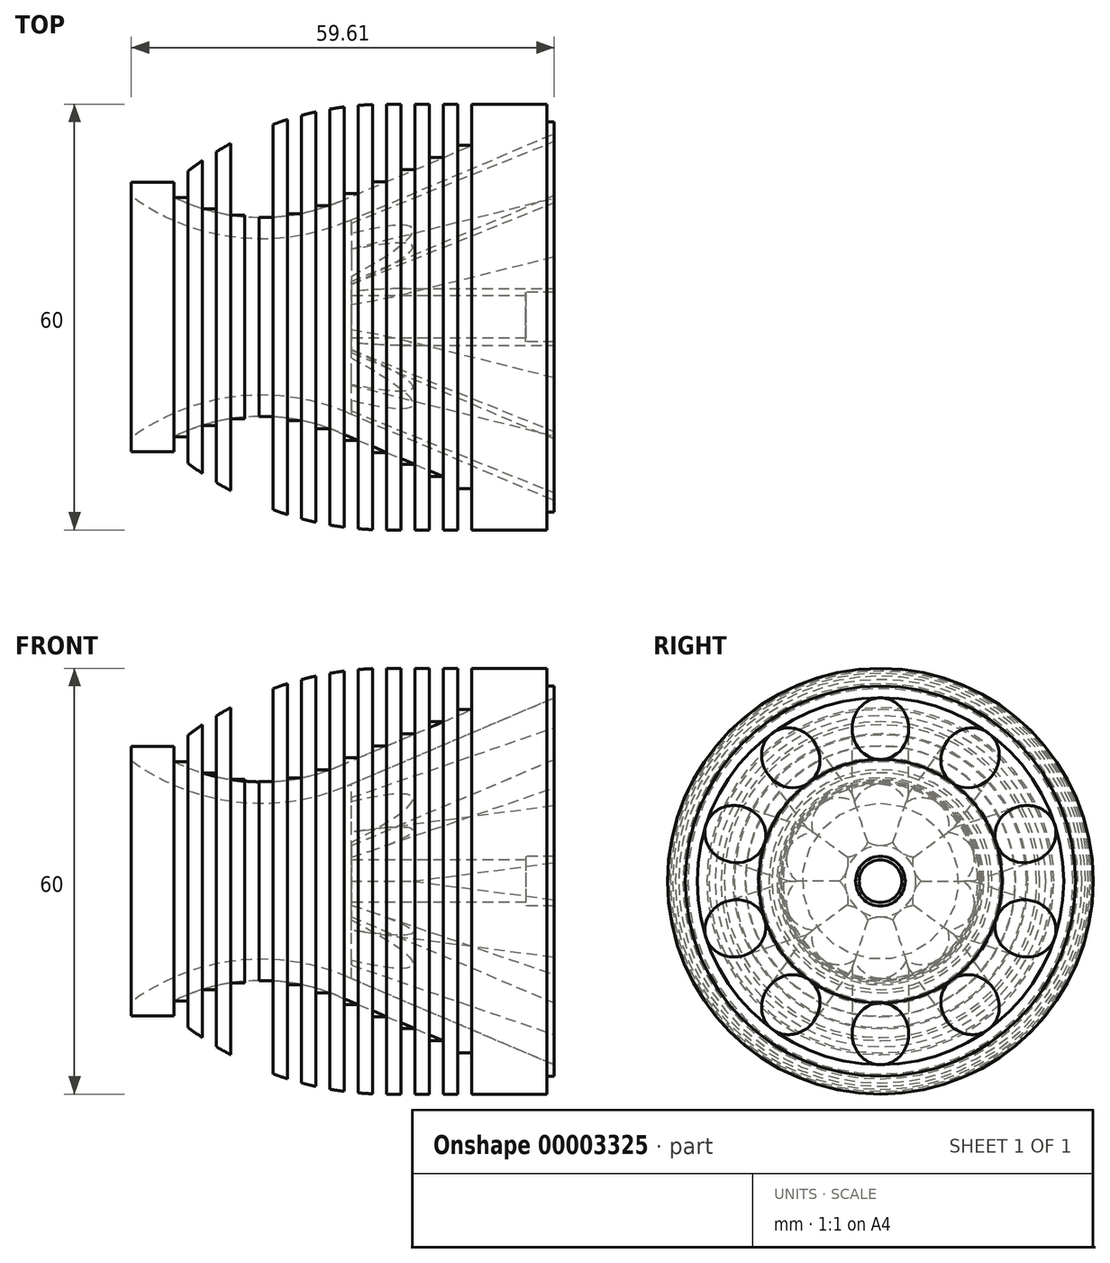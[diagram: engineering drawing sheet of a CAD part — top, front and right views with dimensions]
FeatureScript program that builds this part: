
annotation { "Feature Type Name" : "Feature", "Feature Type Description" : "" }
export const myFeature = defineFeature(function(context is Context, id is Id, definition is map)
    precondition{}
    {
        {
            var Q0;
            Q0=qCreatedBy(makeId("Front.planeOp"),FACE);
            var sketch = newSketch(context, id + "F0", { "sketchPlane" : qUnion([Q0])});
            skLineSegment(sketch, "E0", {"start": v(0, 0) * mm, "end": v(59.61, 0) * mm, "construction": true});
            skLineSegment(sketch, "E1", {"start": v(59.61, 27.5) * mm, "end": v(59.61, -27.5) * mm});
            skLineSegment(sketch, "E2", {"start": v(59.61, 27.5) * mm, "end": v(58.61, 27.5) * mm});
            skLineSegment(sketch, "E3", {"start": v(58.61, 27.5) * mm, "end": v(58.61, 30) * mm});
            skLineSegment(sketch, "E4.0.MirrorCS", {"start": v(58.61, -27.5) * mm, "end": v(58.61, -30) * mm});
            skLineSegment(sketch, "E5.0.MirrorCS", {"start": v(59.61, -27.5) * mm, "end": v(58.61, -27.5) * mm});
            skLineSegment(sketch, "E6", {"start": v(58.61, 30) * mm, "end": v(48, 30) * mm});
            skLineSegment(sketch, "E7.0.MirrorCS", {"start": v(58.61, -30) * mm, "end": v(48, -30) * mm});
            skLineSegment(sketch, "E8", {"start": v(0, 17) * mm, "end": v(0, -17) * mm});
            skLineSegment(sketch, "E9", {"start": v(59.61, 3.5) * mm, "end": v(55.61, 3.5) * mm});
            skLineSegment(sketch, "E10", {"start": v(55.61, 3.5) * mm, "end": v(55.61, 3) * mm});
            skLineSegment(sketch, "E11", {"start": v(55.61, 3) * mm, "end": v(31, 3) * mm});
            skLineSegment(sketch, "E12", {"start": v(31, 3) * mm, "end": v(31, 5) * mm});
            skLineSegment(sketch, "E13", {"start": v(31, 5) * mm, "end": v(59.61, 17.15) * mm});
            skLineSegment(sketch, "E14", {"start": v(59.61, 25.85) * mm, "end": v(30.44, 13.46) * mm});
            skLineSegment(sketch, "E15.0.MirrorCS", {"start": v(59.61, -3.5) * mm, "end": v(55.61, -3.5) * mm});
            skLineSegment(sketch, "E16.0.MirrorCS", {"start": v(55.61, -3.5) * mm, "end": v(55.61, -3) * mm});
            skLineSegment(sketch, "E17.0.MirrorCS", {"start": v(55.61, -3) * mm, "end": v(31, -3) * mm});
            skLineSegment(sketch, "E18.0.MirrorCS", {"start": v(31, -3) * mm, "end": v(31, -5) * mm});
            skLineSegment(sketch, "E19.0.MirrorCS", {"start": v(31, -5) * mm, "end": v(59.61, -17.15) * mm});
            skLineSegment(sketch, "E20.0.MirrorCS", {"start": v(59.61, -25.85) * mm, "end": v(30.44, -13.46) * mm});
            skArc(sketch, "E21", {"start": v(30.44, 13.46) * mm, "mid": v(14.75, 11.2) * mm, "end": v(0, 17) * mm});
            skArc(sketch, "E22.0.MirrorCS", {"start": v(30.44, -13.46) * mm, "mid": v(14.75, -11.2) * mm, "end": v(0, -17) * mm});
            skArc(sketch, "E23.0", {"start": v(29.27, 16.23) * mm, "mid": v(17.57, 14.01) * mm, "end": v(6, 16.86) * mm});
            skLineSegment(sketch, "E23.1", {"start": v(48, 24.18) * mm, "end": v(29.27, 16.23) * mm});
            skLineSegment(sketch, "E24", {"start": v(0, 17) * mm, "end": v(0, 19) * mm});
            skLineSegment(sketch, "E25.0.MirrorCS", {"start": v(48, -24.18) * mm, "end": v(29.27, -16.23) * mm});
            skArc(sketch, "E26.0.MirrorCS", {"start": v(29.27, -16.23) * mm, "mid": v(17.57, -14.01) * mm, "end": v(6, -16.86) * mm});
            skLineSegment(sketch, "E27.0.MirrorCS", {"start": v(0, -17) * mm, "end": v(0, -19) * mm});
            skLineSegment(sketch, "E28", {"start": v(48, 30) * mm, "end": v(48, 24.18) * mm});
            skLineSegment(sketch, "E29.0.MirrorCS", {"start": v(48, -30) * mm, "end": v(48, -24.18) * mm});
            skLineSegment(sketch, "E30", {"start": v(6, -19) * mm, "end": v(6, -16.86) * mm});
            skLineSegment(sketch, "E31.0.MirrorCS", {"start": v(6, 19) * mm, "end": v(6, 16.86) * mm});
            skLineSegment(sketch, "E32", {"start": v(0, 19) * mm, "end": v(6, 19) * mm});
            skLineSegment(sketch, "E33.0.MirrorCS", {"start": v(0, -19) * mm, "end": v(6, -19) * mm});
            skLineSegment(sketch, "E34", {"start": v(31, 5) * mm, "end": v(31, 13.7) * mm});
            skLineSegment(sketch, "E35.0.MirrorCS", {"start": v(31, -5) * mm, "end": v(31, -13.7) * mm});
            skPoint(sketch, "E36", {"position": v(31, 9.36) * mm});
            skLineSegment(sketch, "E37", {"start": v(25.3, 6.93) * mm, "end": v(66.16, 24.28) * mm, "construction": true});
            skPoint(sketch, "E38", {"position": v(59.61, 21.5) * mm});
            skPoint(sketch, "E39.0.MirrorP", {"position": v(59.61, -21.5) * mm});
            skSolve(sketch);
        }
        {
            var Q0;
            Q0=qCreatedBy(makeId("Front.planeOp"),FACE);
            var sketch = newSketch(context, id + "F1", { "sketchPlane" : qUnion([Q0])});
            skLineSegment(sketch, "E40.0", {"start": v(48, 30) * mm, "end": v(48, 24.18) * mm});
            skLineSegment(sketch, "E40.1", {"start": v(48, 24.18) * mm, "end": v(29.27, 16.23) * mm});
            skArc(sketch, "E40.2", {"start": v(29.27, 16.23) * mm, "mid": v(17.57, 14.01) * mm, "end": v(6, 16.86) * mm});
            skLineSegment(sketch, "E40.5", {"start": v(58.61, 30) * mm, "end": v(48, 30) * mm});
            skLineSegment(sketch, "E41", {"start": v(48, 30) * mm, "end": v(36, 30) * mm});
            skArc(sketch, "E42", {"start": v(36, 30) * mm, "mid": v(20.02, 27.16) * mm, "end": v(6, 19) * mm});
            skLineSegment(sketch, "E43", {"start": v(8, 15.98) * mm, "end": v(8, 20.6) * mm});
            skLineSegment(sketch, "E44", {"start": v(10, 15.27) * mm, "end": v(10, 22.03) * mm});
            skLineSegment(sketch, "E45", {"start": v(12, 14.72) * mm, "end": v(12, 23.31) * mm});
            skLineSegment(sketch, "E46", {"start": v(14, 14.34) * mm, "end": v(14, 24.45) * mm});
            skLineSegment(sketch, "E47", {"start": v(16, 14.1) * mm, "end": v(16, 25.47) * mm});
            skLineSegment(sketch, "E48", {"start": v(18, 14) * mm, "end": v(18, 26.37) * mm});
            skLineSegment(sketch, "E49", {"start": v(20, 14.05) * mm, "end": v(20, 27.15) * mm});
            skLineSegment(sketch, "E50", {"start": v(22, 14.24) * mm, "end": v(22, 27.84) * mm});
            skLineSegment(sketch, "E51", {"start": v(24, 14.58) * mm, "end": v(24, 28.42) * mm});
            skLineSegment(sketch, "E52", {"start": v(26, 15.07) * mm, "end": v(26, 28.9) * mm});
            skLineSegment(sketch, "E53", {"start": v(8, 20.6) * mm, "end": v(10, 20.6) * mm, "construction": true});
            skLineSegment(sketch, "E54", {"start": v(10, 22.03) * mm, "end": v(12, 22.03) * mm, "construction": true});
            skLineSegment(sketch, "E55", {"start": v(12, 23.31) * mm, "end": v(14, 23.31) * mm, "construction": true});
            skLineSegment(sketch, "E56", {"start": v(14, 24.45) * mm, "end": v(16, 24.45) * mm, "construction": true});
            skLineSegment(sketch, "E57", {"start": v(16, 25.47) * mm, "end": v(18, 25.47) * mm, "construction": true});
            skLineSegment(sketch, "E58", {"start": v(18, 26.37) * mm, "end": v(20, 26.37) * mm, "construction": true});
            skLineSegment(sketch, "E59", {"start": v(20, 27.15) * mm, "end": v(22, 27.15) * mm, "construction": true});
            skLineSegment(sketch, "E60", {"start": v(22, 27.84) * mm, "end": v(24, 27.84) * mm, "construction": true});
            skLineSegment(sketch, "E61", {"start": v(24, 28.42) * mm, "end": v(26, 28.42) * mm, "construction": true});
            skLineSegment(sketch, "E62", {"start": v(28, 29.3) * mm, "end": v(28, 15.72) * mm});
            skLineSegment(sketch, "E63", {"start": v(32, 29.83) * mm, "end": v(32, 17.38) * mm});
            skLineSegment(sketch, "E64", {"start": v(34, 29.96) * mm, "end": v(34, 18.23) * mm});
            skLineSegment(sketch, "E65", {"start": v(36, 30) * mm, "end": v(36, 19.08) * mm});
            skLineSegment(sketch, "E66", {"start": v(38, 30) * mm, "end": v(38, 19.93) * mm});
            skLineSegment(sketch, "E67", {"start": v(40, 30) * mm, "end": v(40, 20.78) * mm});
            skLineSegment(sketch, "E68", {"start": v(42, 30) * mm, "end": v(42, 21.63) * mm});
            skLineSegment(sketch, "E69", {"start": v(26, 22) * mm, "end": v(28, 22) * mm, "construction": true});
            skLineSegment(sketch, "E70", {"start": v(28, 22.51) * mm, "end": v(30, 22.51) * mm, "construction": true});
            skLineSegment(sketch, "E71", {"start": v(30, 23.07) * mm, "end": v(32, 23.07) * mm, "construction": true});
            skLineSegment(sketch, "E72", {"start": v(32, 23.6) * mm, "end": v(34, 23.6) * mm, "construction": true});
            skLineSegment(sketch, "E73", {"start": v(34, 24.1) * mm, "end": v(36, 24.1) * mm, "construction": true});
            skLineSegment(sketch, "E74", {"start": v(36, 24.54) * mm, "end": v(38, 24.54) * mm, "construction": true});
            skLineSegment(sketch, "E75", {"start": v(38, 24.97) * mm, "end": v(40, 24.97) * mm, "construction": true});
            skLineSegment(sketch, "E76", {"start": v(40, 25.4) * mm, "end": v(42, 25.4) * mm, "construction": true});
            skLineSegment(sketch, "E77", {"start": v(44, 22.48) * mm, "end": v(44, 30) * mm});
            skLineSegment(sketch, "E78", {"start": v(46, 23.33) * mm, "end": v(46, 30) * mm});
            skLineSegment(sketch, "E79", {"start": v(42, 25.81) * mm, "end": v(44, 25.81) * mm, "construction": true});
            skLineSegment(sketch, "E80", {"start": v(44, 26.24) * mm, "end": v(46, 26.24) * mm, "construction": true});
            skLineSegment(sketch, "E81.0", {"start": v(6, 19) * mm, "end": v(6, 16.86) * mm});
            skLineSegment(sketch, "E81.1", {"start": v(0, 19) * mm, "end": v(6, 19) * mm});
            skLineSegment(sketch, "E81.2", {"start": v(0, 17) * mm, "end": v(0, 19) * mm});
            skLineSegment(sketch, "E82", {"start": v(30, 29.61) * mm, "end": v(30, 16.54) * mm});
            skLineSegment(sketch, "E83", {"start": v(6, 16.86) * mm, "end": v(8, 16.86) * mm});
            skLineSegment(sketch, "E84", {"start": v(10, 15.27) * mm, "end": v(12, 15.27) * mm});
            skLineSegment(sketch, "E85", {"start": v(14, 14.34) * mm, "end": v(16, 14.34) * mm});
            skLineSegment(sketch, "E86", {"start": v(20, 14.05) * mm, "end": v(18, 14.05) * mm});
            skLineSegment(sketch, "E87", {"start": v(24, 14.58) * mm, "end": v(22, 14.58) * mm});
            skLineSegment(sketch, "E88", {"start": v(28, 15.72) * mm, "end": v(26, 15.72) * mm});
            skLineSegment(sketch, "E89", {"start": v(32, 17.38) * mm, "end": v(30, 17.38) * mm});
            skLineSegment(sketch, "E90", {"start": v(36, 19.08) * mm, "end": v(34, 19.08) * mm});
            skLineSegment(sketch, "E91", {"start": v(40, 20.78) * mm, "end": v(38, 20.78) * mm});
            skLineSegment(sketch, "E92", {"start": v(44, 22.48) * mm, "end": v(42, 22.48) * mm});
            skLineSegment(sketch, "E93", {"start": v(48, 24.18) * mm, "end": v(46, 24.18) * mm});
            skSolve(sketch);
        }
        {
            var Q0;
            {var subQ5=sQuery(id+"F0.wireOp",EDGE,"E2");Q0=makeQuery(id+"F0.imprint","IMPRINT",FACE,{"disambiguationData":[TD([[makeQuery(id+"F0.imprint","IMPRINT",EDGE,{"derivedFrom":subQ5}),1.0]])]});}
            var Q1;
            {var subQ1=sQuery(id+"F0.wireOp",EDGE,"E9");Q1=makeQuery(id+"F0.imprint","IMPRINT",FACE,{"disambiguationData":[TD([[makeQuery(id+"F0.imprint","IMPRINT",EDGE,{"derivedFrom":subQ1}),-1.0]])]});}
            var Q2;
            {var subQ1=sQuery(id+"F0.wireOp",EDGE,"E15.0.MirrorCS");Q2=makeQuery(id+"F0.imprint","IMPRINT",FACE,{"disambiguationData":[TD([[makeQuery(id+"F0.imprint","IMPRINT",EDGE,{"derivedFrom":subQ1}),1.0]])]});}
            var Q3;
            Q3=makeQuery(id+"F0.imprint","IMPRINT",FACE,{"disambiguationData":[TD([[makeQuery(id+"F0.imprint","IMPRINT",EDGE,{"derivedFrom":sQuery(id+"F0.wireOp",EDGE,"E4.0.MirrorCS")}),-1.0]])]});
            var Q4;
            {var subQ5=sQuery(id+"F0.wireOp",EDGE,"E2");Q4=makeQuery(id+"F0.imprint","IMPRINT",FACE,{"disambiguationData":[TD([[makeQuery(id+"F0.imprint","IMPRINT",EDGE,{"derivedFrom":subQ5}),1.0]])]});}
            var Q5;
            Q5=makeQuery(id+"F0.imprint","IMPRINT",FACE,{"disambiguationData":[TD([[makeQuery(id+"F0.imprint","IMPRINT",EDGE,{"derivedFrom":sQuery(id+"F0.wireOp",EDGE,"E4.0.MirrorCS")}),-1.0]])]});
            var Q6;
            {var subQ0=sQuery(id+"F1.wireOp",EDGE,"E44");Q6=makeQuery(id+"F1.imprint","IMPRINT",FACE,{"disambiguationData":[TD([[makeQuery(id+"F1.imprint","IMPRINT",EDGE,{"derivedFrom":subQ0}),1.0]])]});}
            var Q7;
            {var subQ0=sQuery(id+"F1.wireOp",EDGE,"E46");Q7=makeQuery(id+"F1.imprint","IMPRINT",FACE,{"disambiguationData":[TD([[makeQuery(id+"F1.imprint","IMPRINT",EDGE,{"derivedFrom":subQ0}),1.0]])]});}
            var Q8;
            {var subQ2=sQuery(id+"F1.wireOp",EDGE,"E40.2");var subQ4=sQuery(id+"F1.wireOp",EDGE,"E47");var subQ8=makeQuery(id+"F1.imprint","INTERSECT",VERTEX,{"derivedFrom":[subQ2,subQ4]});Q8=makeQuery(id+"F1.imprint","IMPRINT",FACE,{"disambiguationData":[TD([[makeQuery(id+"F1.imprint","IMPRINT",EDGE,{"disambiguationData":[TD([[subQ8,1.0]])],"derivedFrom":subQ2}),-1.0]])]});}
            var Q9;
            {var subQ6=sQuery(id+"F1.wireOp",EDGE,"E49");Q9=makeQuery(id+"F1.imprint","IMPRINT",FACE,{"disambiguationData":[TD([[makeQuery(id+"F1.imprint","IMPRINT",EDGE,{"derivedFrom":subQ6}),-1.0]])]});}
            var Q10;
            {var subQ6=sQuery(id+"F1.wireOp",EDGE,"E51");Q10=makeQuery(id+"F1.imprint","IMPRINT",FACE,{"disambiguationData":[TD([[makeQuery(id+"F1.imprint","IMPRINT",EDGE,{"derivedFrom":subQ6}),-1.0]])]});}
            var Q11;
            {var subQ6=sQuery(id+"F1.wireOp",EDGE,"E62");Q11=makeQuery(id+"F1.imprint","IMPRINT",FACE,{"disambiguationData":[TD([[makeQuery(id+"F1.imprint","IMPRINT",EDGE,{"derivedFrom":subQ6}),1.0]])]});}
            var Q12;
            {var subQ6=sQuery(id+"F1.wireOp",EDGE,"E63");Q12=makeQuery(id+"F1.imprint","IMPRINT",FACE,{"disambiguationData":[TD([[makeQuery(id+"F1.imprint","IMPRINT",EDGE,{"derivedFrom":subQ6}),1.0]])]});}
            var Q13;
            {var subQ6=sQuery(id+"F1.wireOp",EDGE,"E65");Q13=makeQuery(id+"F1.imprint","IMPRINT",FACE,{"disambiguationData":[TD([[makeQuery(id+"F1.imprint","IMPRINT",EDGE,{"derivedFrom":subQ6}),1.0]])]});}
            var Q14;
            {var subQ6=sQuery(id+"F1.wireOp",EDGE,"E67");Q14=makeQuery(id+"F1.imprint","IMPRINT",FACE,{"disambiguationData":[TD([[makeQuery(id+"F1.imprint","IMPRINT",EDGE,{"derivedFrom":subQ6}),1.0]])]});}
            var Q15;
            {var subQ4=sQuery(id+"F1.wireOp",EDGE,"E77");Q15=makeQuery(id+"F1.imprint","IMPRINT",FACE,{"disambiguationData":[TD([[makeQuery(id+"F1.imprint","IMPRINT",EDGE,{"derivedFrom":subQ4}),-1.0]])]});}
            var Q16;
            {var subQ4=sQuery(id+"F0.wireOp",EDGE,"E13");Q16=makeQuery(id+"F0.imprint","IMPRINT",FACE,{"disambiguationData":[TD([[makeQuery(id+"F0.imprint","IMPRINT",EDGE,{"derivedFrom":subQ4}),1.0]])]});}
            var Q17;
            {var subQ0=sQuery(id+"F1.wireOp",EDGE,"E83");Q17=makeQuery(id+"F1.imprint","IMPRINT",FACE,{"disambiguationData":[TD([[makeQuery(id+"F1.imprint","IMPRINT",EDGE,{"derivedFrom":subQ0}),-1.0]])]});}
            var Q18;
            {var subQ0=sQuery(id+"F1.wireOp",EDGE,"E84");Q18=makeQuery(id+"F1.imprint","IMPRINT",FACE,{"disambiguationData":[TD([[makeQuery(id+"F1.imprint","IMPRINT",EDGE,{"derivedFrom":subQ0}),-1.0]])]});}
            var Q19;
            {var subQ0=sQuery(id+"F1.wireOp",EDGE,"E85");Q19=makeQuery(id+"F1.imprint","IMPRINT",FACE,{"disambiguationData":[TD([[makeQuery(id+"F1.imprint","IMPRINT",EDGE,{"derivedFrom":subQ0}),-1.0]])]});}
            var Q20;
            {var subQ0=sQuery(id+"F1.wireOp",EDGE,"E86");Q20=makeQuery(id+"F1.imprint","IMPRINT",FACE,{"disambiguationData":[TD([[makeQuery(id+"F1.imprint","IMPRINT",EDGE,{"derivedFrom":subQ0}),1.0]])]});}
            var Q21;
            {var subQ0=sQuery(id+"F1.wireOp",EDGE,"E87");Q21=makeQuery(id+"F1.imprint","IMPRINT",FACE,{"disambiguationData":[TD([[makeQuery(id+"F1.imprint","IMPRINT",EDGE,{"derivedFrom":subQ0}),1.0]])]});}
            var Q22;
            {var subQ0=sQuery(id+"F1.wireOp",EDGE,"E88");Q22=makeQuery(id+"F1.imprint","IMPRINT",FACE,{"disambiguationData":[TD([[makeQuery(id+"F1.imprint","IMPRINT",EDGE,{"derivedFrom":subQ0}),1.0]])]});}
            var Q23;
            {var subQ0=sQuery(id+"F1.wireOp",EDGE,"E89");Q23=makeQuery(id+"F1.imprint","IMPRINT",FACE,{"disambiguationData":[TD([[makeQuery(id+"F1.imprint","IMPRINT",EDGE,{"derivedFrom":subQ0}),1.0]])]});}
            var Q24;
            {var subQ0=sQuery(id+"F1.wireOp",EDGE,"E90");Q24=makeQuery(id+"F1.imprint","IMPRINT",FACE,{"disambiguationData":[TD([[makeQuery(id+"F1.imprint","IMPRINT",EDGE,{"derivedFrom":subQ0}),1.0]])]});}
            var Q25;
            {var subQ0=sQuery(id+"F1.wireOp",EDGE,"E91");Q25=makeQuery(id+"F1.imprint","IMPRINT",FACE,{"disambiguationData":[TD([[makeQuery(id+"F1.imprint","IMPRINT",EDGE,{"derivedFrom":subQ0}),1.0]])]});}
            var Q26;
            {var subQ0=sQuery(id+"F1.wireOp",EDGE,"E92");Q26=makeQuery(id+"F1.imprint","IMPRINT",FACE,{"disambiguationData":[TD([[makeQuery(id+"F1.imprint","IMPRINT",EDGE,{"derivedFrom":subQ0}),1.0]])]});}
            var Q27;
            {var subQ0=sQuery(id+"F1.wireOp",EDGE,"E93");Q27=makeQuery(id+"F1.imprint","IMPRINT",FACE,{"disambiguationData":[TD([[makeQuery(id+"F1.imprint","IMPRINT",EDGE,{"derivedFrom":subQ0}),1.0]])]});}
            var Q28;
            Q28=sQuery(id+"F0.wireOp",EDGE,"E0");
            revolve(context, id + "F2", {"entities" : qUnion([Q0, Q1, Q2, Q3, Q4, Q5, Q6, Q7, Q8, Q9, Q10, Q11, Q12, Q13, Q14, Q15, Q16, Q17, Q18, Q19, Q20, Q21, Q22, Q23, Q24, Q25, Q26, Q27]), "axis" : qUnion([Q28]), "revolveType" : RevolveType.FULL});
        }
        {
            var Q0;
            Q0=sQuery(id+"F0.wireOp",EDGE,"E37");
            var Q1;
            Q1=sQuery(id+"F0.wireOp",VERTEX,"E37.end");
            cPlane(context, id + "F3", {"entities" : qUnion([Q0, Q1]), "cplaneType" : CPlaneType.LINE_POINT, "offset" : 150 * mm, "width" : 150 * mm, "height" : 150 * mm});
        }
        {
            var Q0;
            Q0=qCreatedBy(id+"F3.planeOp",FACE);
            var sketch = newSketch(context, id + "F4", { "sketchPlane" : qUnion([Q0])});
            skPoint(sketch, "E94.0", {"position": v(0, -3.5) * mm});
            skCircle(sketch, "E95", {"center": v(0, -3.5) * mm, "radius": 4 * mm});
            skSolve(sketch);
        }
        {
            var Q0;
            Q0=makeQuery(id+"F4.imprint","IMPRINT",FACE,{"disambiguationData":[TD([[makeQuery(id+"F4.imprint","IMPRINT",EDGE,{"derivedFrom":sQuery(id+"F4.wireOp",EDGE,"E95")}),1.0]])]});
            extrude(context, id + "F5", {"entities" : qUnion([Q0]), "operationType" : NewBodyOperationType.REMOVE, "oppositeDirection" : true, "depth" : 45 * mm});
        }
        {
            var Q0;
            Q0=makeQuery(id+"F5.boolean.opBoolean","COPY",FACE,{"derivedFrom":makeQuery(id+"F5.opExtrude","SWEPT_FACE",FACE,{"disambiguationData":[OSD([sQuery(id+"F4.wireOp",EDGE,"E95")])]})});
            var Q1;
            Q1=makeQuery(id+"F2.opRevolve","SWEPT_FACE",FACE,{"disambiguationData":[OSD([sQuery(id+"F0.wireOp",EDGE,"E11")])]});
            circularPattern(context, id + "F6", {"faces" : qUnion([Q0]), "axis" : qUnion([Q1]), "angle" : 36 * degree, "instanceCount" : 10, "patternType" : PatternType.FACE});
        }
    });
